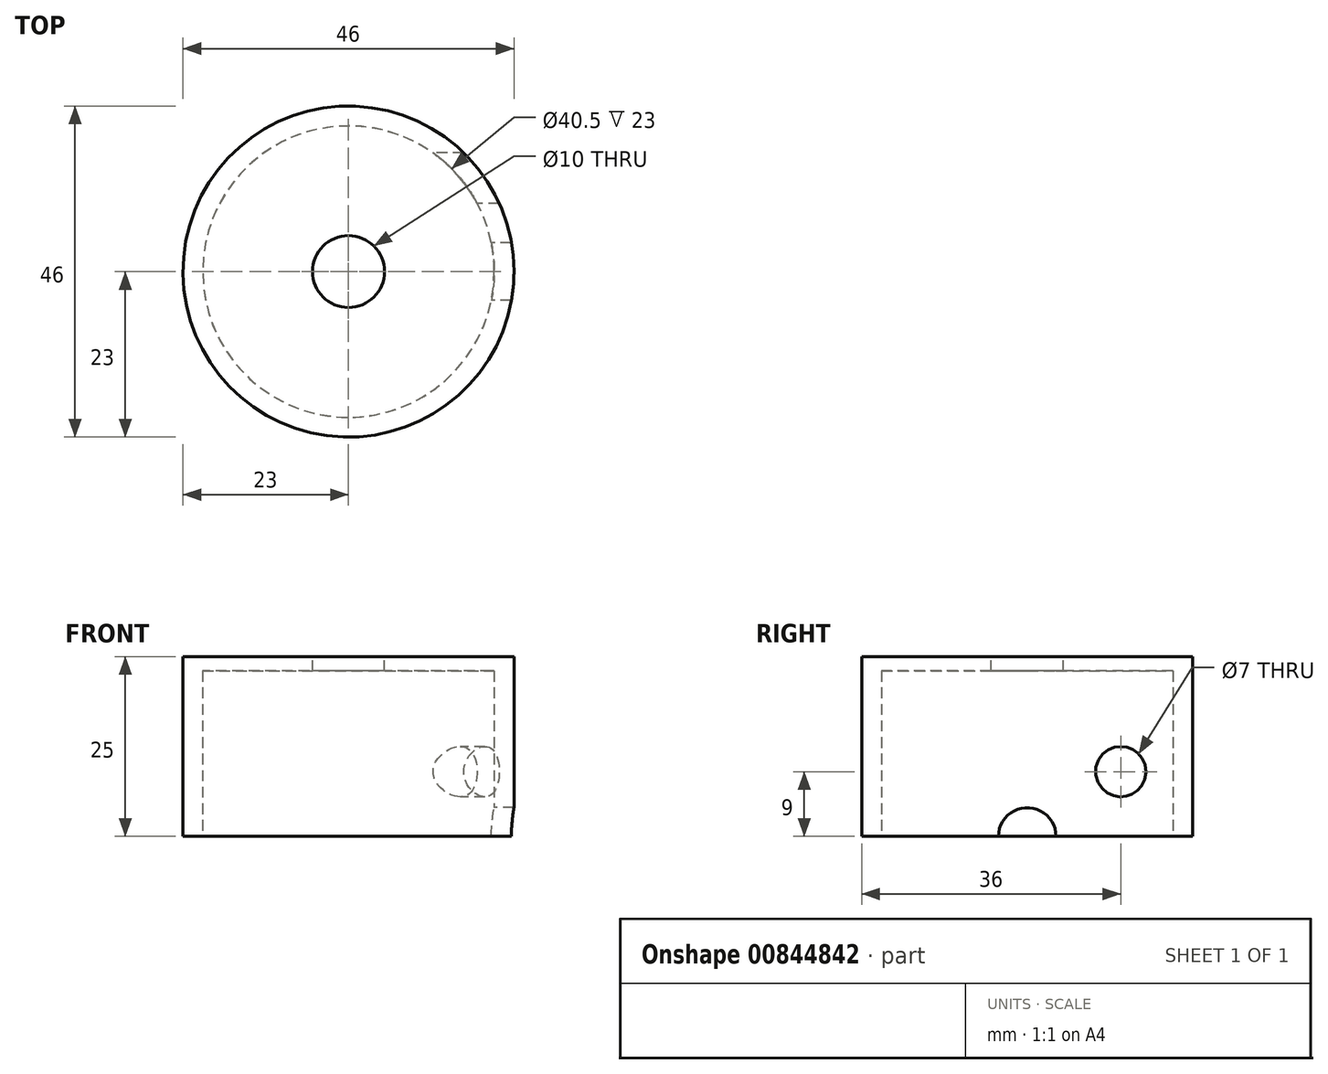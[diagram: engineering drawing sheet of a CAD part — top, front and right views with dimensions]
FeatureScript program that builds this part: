
annotation { "Feature Type Name" : "Feature", "Feature Type Description" : "" }
export const myFeature = defineFeature(function(context is Context, id is Id, definition is map)
    precondition{}
    {
        {
            var Q0;
            Q0=qCreatedBy(makeId("Top.planeOp"),FACE);
            var sketch = newSketch(context, id + "F0", { "sketchPlane" : qUnion([Q0])});
            skCircle(sketch, "E0", {"center": v(0, 0) * mm, "radius": 23 * mm});
            skCircle(sketch, "E1", {"center": v(0, 0) * mm, "radius": 20.25 * mm});
            skSolve(sketch);
        }
        {
            var Q0;
            Q0=makeQuery(id+"F0.imprint","IMPRINT",FACE,{"disambiguationData":[TD([[makeQuery(id+"F0.imprint","IMPRINT",EDGE,{"derivedFrom":sQuery(id+"F0.wireOp",EDGE,"E0")}),1.0]])]});
            extrude(context, id + "F1", {"entities" : qUnion([Q0]), "depth" : 23 * mm, "offsetDistance" : 25 * mm});
        }
        {
            var Q0;
            Q0=makeQuery(id+"F1.opExtrude","CAP_FACE",FACE,{"disambiguationData":[OSD([sQuery(id+"F0.wireOp",EDGE,"E0"),sQuery(id+"F0.wireOp",EDGE,"E1")])],"isStart":false});
            var sketch = newSketch(context, id + "F2", { "sketchPlane" : qUnion([Q0])});
            skCircle(sketch, "E2", {"center": v(0, 0) * mm, "radius": 23 * mm});
            skSolve(sketch);
        }
        {
            var Q0;
            Q0=makeQuery(id+"F2.imprint","IMPRINT",FACE,{"disambiguationData":[TD([[makeQuery(id+"F2.imprint","IMPRINT",EDGE,{"derivedFrom":sQuery(id+"F2.wireOp",EDGE,"E2")}),1.0]])]});
            var Q1;
            Q1=makeQuery(id+"F2.imprint","IMPRINT",FACE,{"disambiguationData":[TD([[makeQuery(id+"F2.imprint","IMPRINT",EDGE,{"derivedFrom":makeQuery(id+"F1.opExtrude","CAP_EDGE",EDGE,{"disambiguationData":[OSD([sQuery(id+"F0.wireOp",EDGE,"E1")])],"isStart":false})}),1.0]])]});
            extrude(context, id + "F3", {"entities" : qUnion([Q0, Q1]), "operationType" : NewBodyOperationType.ADD, "depth" : 2 * mm, "offsetDistance" : 25 * mm});
        }
        {
            var Q0;
            Q0=makeQuery(id+"F3.opExtrude","CAP_FACE",FACE,{"disambiguationData":[OSD([sQuery(id+"F2.wireOp",EDGE,"E2")])],"isStart":false});
            var sketch = newSketch(context, id + "F4", { "sketchPlane" : qUnion([Q0])});
            skCircle(sketch, "E3", {"center": v(0, 0) * mm, "radius": 5 * mm});
            skSolve(sketch);
        }
        {
            var Q0;
            Q0=makeQuery(id+"F4.imprint","IMPRINT",FACE,{"disambiguationData":[TD([[makeQuery(id+"F4.imprint","IMPRINT",EDGE,{"derivedFrom":sQuery(id+"F4.wireOp",EDGE,"E3")}),1.0]])]});
            var Q1;
            Q1=sQuery(id+"F4.wireOp",EDGE,"E3");
            extrude(context, id + "F5", {"entities" : qUnion([Q0]), "operationType" : NewBodyOperationType.REMOVE, "surfaceEntities" : qUnion([Q1]), "oppositeDirection" : true, "depth" : 3 * mm, "offsetDistance" : 25 * mm});
        }
        {
            var Q0;
            Q0=qCreatedBy(makeId("Right.planeOp"),FACE);
            var sketch = newSketch(context, id + "F6", { "sketchPlane" : qUnion([Q0])});
            skCircle(sketch, "E4", {"center": v(0, 0) * mm, "radius": 4 * mm});
            skPoint(sketch, "E5", {"position": v(-4, 0) * mm});
            skCircle(sketch, "E6", {"center": v(13, 9) * mm, "radius": 3.5 * mm});
            skLineSegment(sketch, "E7", {"start": v(13, 15.2) * mm, "end": v(13, 3.63) * mm, "construction": true});
            skLineSegment(sketch, "E8", {"start": v(0, 5.36) * mm, "end": v(0, -6.31) * mm, "construction": true});
            skFitSpline(sketch, "E9", {"points": [v(-4, 0) * mm, v(13, 12.5) * mm, v(15.2, 11.72) * mm, v(15.2, 11.72) * mm, v(16.3, 10.14) * mm, v(15.87, 7) * mm, v(13, 5.5) * mm, v(4, 0) * mm], "startDerivative": vector(9.76, 87.6) * mm, "endDerivative": vector(-44.26, -88.04) * mm});
            skSolve(sketch);
        }
        {
            var Q0;
            Q0=makeQuery(id+"F6.imprint","IMPRINT",FACE,{"disambiguationData":[TD([[makeQuery(id+"F6.imprint","IMPRINT",EDGE,{"derivedFrom":sQuery(id+"F6.wireOp",EDGE,"E4")}),1.0]])]});
            extrude(context, id + "F7", {"entities" : qUnion([Q0]), "operationType" : NewBodyOperationType.REMOVE, "depth" : 400 * mm, "offsetDistance" : 25 * mm});
        }
        {
            var Q0;
            Q0=qSketchRegion(id+"F6",true);
            extrude(context, id + "F8", {"entities" : qUnion([Q0]), "operationType" : NewBodyOperationType.REMOVE, "depth" : 100 * mm, "offsetDistance" : 25 * mm});
        }
    });
